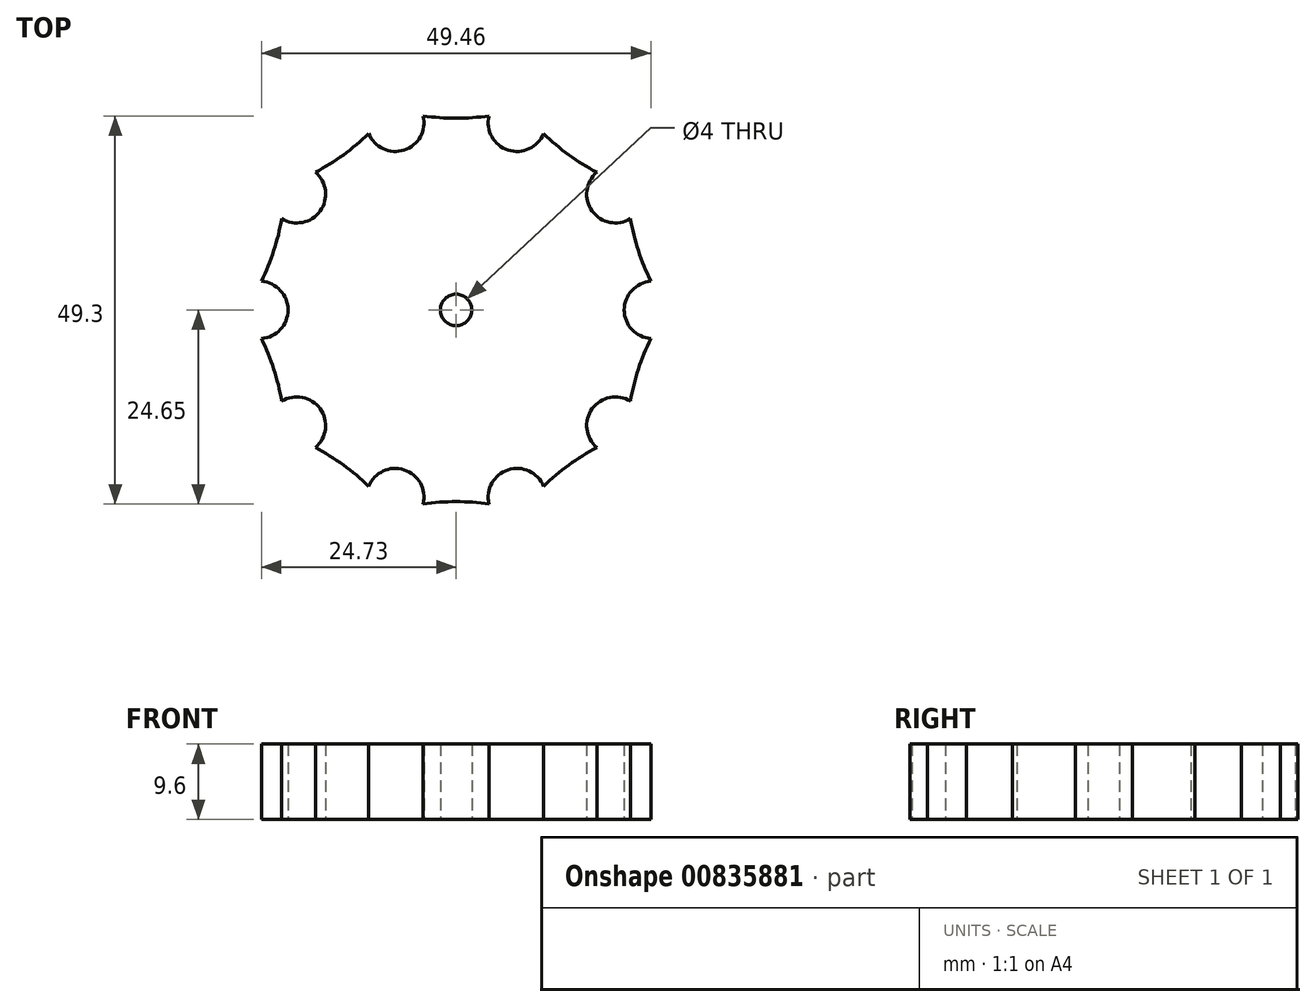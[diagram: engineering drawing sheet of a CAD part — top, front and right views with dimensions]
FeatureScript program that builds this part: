
annotation { "Feature Type Name" : "Feature", "Feature Type Description" : "" }
export const myFeature = defineFeature(function(context is Context, id is Id, definition is map)
    precondition{}
    {
        {
            var Q0;
            Q0=qCreatedBy(makeId("Top.planeOp"),FACE);
            var sketch = newSketch(context, id + "F0", { "sketchPlane" : qUnion([Q0])});
            skCircle(sketch, "E0", {"center": v(0, 0) * mm, "radius": 25 * mm});
            skArc(sketch, "E1", {"start": v(24.73, 3.64) * mm, "mid": v(21.36, 0) * mm, "end": v(24.73, -3.64) * mm});
            skArc(sketch, "E2.1.0", {"start": v(17.87, 17.48) * mm, "mid": v(17.28, 12.55) * mm, "end": v(22.15, 11.6) * mm});
            skArc(sketch, "E2.2.0", {"start": v(4.18, 24.65) * mm, "mid": v(6.6, 20.3) * mm, "end": v(11.1, 22.4) * mm});
            skArc(sketch, "E2.3.0", {"start": v(-11.1, 22.4) * mm, "mid": v(-6.6, 20.3) * mm, "end": v(-4.18, 24.65) * mm});
            skArc(sketch, "E2.4.0", {"start": v(-22.15, 11.6) * mm, "mid": v(-17.28, 12.55) * mm, "end": v(-17.87, 17.48) * mm});
            skArc(sketch, "E2.5.0", {"start": v(-24.73, -3.64) * mm, "mid": v(-21.36, 0) * mm, "end": v(-24.73, 3.64) * mm});
            skArc(sketch, "E2.6.0", {"start": v(-17.87, -17.48) * mm, "mid": v(-17.28, -12.55) * mm, "end": v(-22.15, -11.6) * mm});
            skArc(sketch, "E2.7.0", {"start": v(-4.18, -24.65) * mm, "mid": v(-6.6, -20.3) * mm, "end": v(-11.1, -22.4) * mm});
            skArc(sketch, "E2.8.0", {"start": v(11.1, -22.4) * mm, "mid": v(6.6, -20.3) * mm, "end": v(4.18, -24.65) * mm});
            skArc(sketch, "E2.9.0", {"start": v(22.15, -11.6) * mm, "mid": v(17.28, -12.55) * mm, "end": v(17.87, -17.48) * mm});
            skArc(sketch, "E3", {"start": v(22.15, 11.6) * mm, "mid": v(23.16, 7.52) * mm, "end": v(24.73, 3.64) * mm});
            skArc(sketch, "E4.1.0", {"start": v(11.1, 22.4) * mm, "mid": v(14.31, 19.7) * mm, "end": v(17.87, 17.48) * mm});
            skArc(sketch, "E4.2.0", {"start": v(-4.18, 24.65) * mm, "mid": v(0, 24.35) * mm, "end": v(4.18, 24.65) * mm});
            skArc(sketch, "E4.3.0", {"start": v(-17.87, 17.48) * mm, "mid": v(-14.31, 19.7) * mm, "end": v(-11.1, 22.4) * mm});
            skArc(sketch, "E4.4.0", {"start": v(-24.73, 3.64) * mm, "mid": v(-23.16, 7.52) * mm, "end": v(-22.15, 11.6) * mm});
            skArc(sketch, "E4.5.0", {"start": v(-22.15, -11.6) * mm, "mid": v(-23.16, -7.52) * mm, "end": v(-24.73, -3.64) * mm});
            skArc(sketch, "E4.6.0", {"start": v(-11.1, -22.4) * mm, "mid": v(-14.31, -19.7) * mm, "end": v(-17.87, -17.48) * mm});
            skArc(sketch, "E4.7.0", {"start": v(4.18, -24.65) * mm, "mid": v(0, -24.35) * mm, "end": v(-4.18, -24.65) * mm});
            skArc(sketch, "E4.8.0", {"start": v(17.87, -17.48) * mm, "mid": v(14.31, -19.7) * mm, "end": v(11.1, -22.4) * mm});
            skArc(sketch, "E4.9.0", {"start": v(24.73, -3.64) * mm, "mid": v(23.16, -7.52) * mm, "end": v(22.15, -11.6) * mm});
            skCircle(sketch, "E5", {"center": v(0, 0) * mm, "radius": 2 * mm});
            skSolve(sketch);
        }
        {
            var Q0;
            Q0=makeQuery(id+"F0.imprint","IMPRINT",FACE,{"disambiguationData":[TD([[makeQuery(id+"F0.imprint","IMPRINT",EDGE,{"derivedFrom":sQuery(id+"F0.wireOp",EDGE,"E1")}),-1.0]])]});
            extrude(context, id + "F1", {"entities" : qUnion([Q0]), "depth" : 9.6 * mm, "offsetDistance" : 25 * mm});
        }
    });
